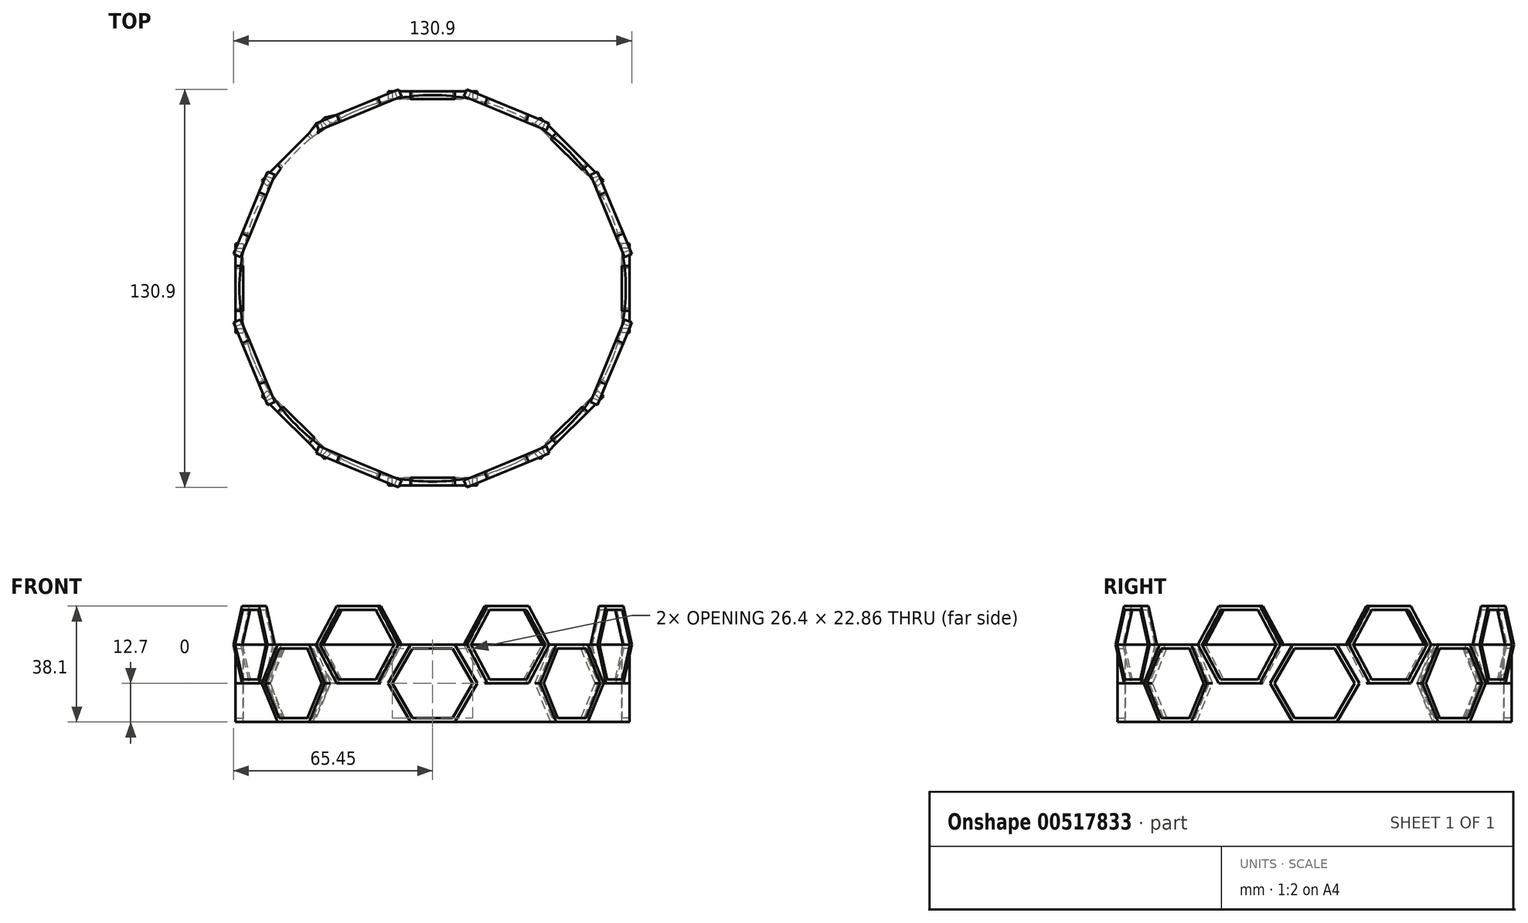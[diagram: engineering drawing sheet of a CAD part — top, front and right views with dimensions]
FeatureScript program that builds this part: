
annotation { "Feature Type Name" : "Feature", "Feature Type Description" : "" }
export const myFeature = defineFeature(function(context is Context, id is Id, definition is map)
    precondition{}
    {
        {
            var Q0;
            Q0=qCreatedBy(makeId("Top.planeOp"),FACE);
            var sketch = newSketch(context, id + "F0", { "sketchPlane" : qUnion([Q0])});
            skCircle(sketch, "E0", {"center": v(0, 0) * mm, "radius": 63.5 * mm});
            skLineSegment(sketch, "E1", {"start": v(-60.89, -18.03) * mm, "end": v(19.66, 60.38) * mm});
            skSolve(sketch);
        }
        {
            var Q0;
            {var subQ0=sQuery(id+"F0.wireOp",EDGE,"E1");Q0=makeQuery(id+"F0.imprint","IMPRINT",FACE,{"disambiguationData":[TD([[makeQuery(id+"F0.imprint","IMPRINT",EDGE,{"derivedFrom":subQ0}),1.0]])]});}
            var Q1;
            {var subQ0=sQuery(id+"F0.wireOp",EDGE,"E1");Q1=makeQuery(id+"F0.imprint","IMPRINT",FACE,{"disambiguationData":[TD([[makeQuery(id+"F0.imprint","IMPRINT",EDGE,{"derivedFrom":subQ0}),-1.0]])]});}
            extrude(context, id + "F1", {"entities" : qUnion([Q0, Q1]), "depth" : 25.4 * mm, "offsetDistance" : 25.4 * mm});
        }
        {
            var Q0;
            Q0=makeQuery(id+"F1.opExtrude","CAP_FACE",FACE,{"disambiguationData":[OSD([sQuery(id+"F0.wireOp",EDGE,"E0")])],"isStart":true});
            var sketch = newSketch(context, id + "F2", { "sketchPlane" : qUnion([Q0])});
            skLineSegment(sketch, "E2", {"start": v(0, 0) * mm, "end": v(63.5, 0) * mm});
            skSolve(sketch);
        }
        {
            var Q0;
            Q0=sQuery(id+"F2.wireOp",VERTEX,"E2.end");
            var Q1;
            Q1=sQuery(id+"F2.wireOp",EDGE,"E2");
            cPlane(context, id + "F3", {"entities" : qUnion([Q0, Q1]), "cplaneType" : CPlaneType.LINE_POINT, "offset" : 25.4 * mm, "width" : 152.4 * mm, "height" : 152.4 * mm});
        }
        {
            var Q0;
            Q0=qCreatedBy(id+"F3.planeOp",FACE);
            var sketch = newSketch(context, id + "F4", { "sketchPlane" : qUnion([Q0])});
            skPoint(sketch, "E3", {"position": v(0, 12.7) * mm});
            skCircle(sketch, "E4.cCircle", {"center": v(0, 12.7) * mm, "radius": 12.7 * mm, "construction": true});
            skLineSegment(sketch, "E4.0", {"start": v(7.33, 25.4) * mm, "end": v(14.66, 12.7) * mm});
            skLineSegment(sketch, "E4.1", {"start": v(14.66, 12.7) * mm, "end": v(7.33, 0) * mm});
            skLineSegment(sketch, "E4.2", {"start": v(7.33, 0) * mm, "end": v(-7.33, 0) * mm});
            skLineSegment(sketch, "E4.3", {"start": v(-7.33, 0) * mm, "end": v(-14.66, 12.7) * mm});
            skLineSegment(sketch, "E4.4", {"start": v(-14.66, 12.7) * mm, "end": v(-7.33, 25.4) * mm});
            skLineSegment(sketch, "E4.5", {"start": v(-7.33, 25.4) * mm, "end": v(7.33, 25.4) * mm});
            skPoint(sketch, "E4.0.midPoint", {"position": v(11, 19.05) * mm});
            skPoint(sketch, "E5", {"position": v(0, 0) * mm});
            skCircle(sketch, "E6.cCircle", {"center": v(0, 12.7) * mm, "radius": 13.2 * mm, "construction": true});
            skLineSegment(sketch, "E6.0", {"start": v(6.6, 1.27) * mm, "end": v(-6.6, 1.27) * mm});
            skLineSegment(sketch, "E6.1", {"start": v(-6.6, 1.27) * mm, "end": v(-13.2, 12.7) * mm});
            skLineSegment(sketch, "E6.2", {"start": v(-13.2, 12.7) * mm, "end": v(-6.6, 24.13) * mm});
            skLineSegment(sketch, "E6.3", {"start": v(-6.6, 24.13) * mm, "end": v(6.6, 24.13) * mm});
            skLineSegment(sketch, "E6.4", {"start": v(6.6, 24.13) * mm, "end": v(13.2, 12.7) * mm});
            skLineSegment(sketch, "E6.5", {"start": v(13.2, 12.7) * mm, "end": v(6.6, 1.27) * mm});
            skSolve(sketch);
        }
        {
            var Q0;
            Q0=makeQuery(id+"F4.imprint","IMPRINT",FACE,{"disambiguationData":[TD([[makeQuery(id+"F4.imprint","IMPRINT",EDGE,{"derivedFrom":sQuery(id+"F4.wireOp",EDGE,"E4.0")}),-1.0]])]});
            extrude(context, id + "F5", {"entities" : qUnion([Q0]), "depth" : 1.27 * mm, "offsetDistance" : 25.4 * mm, "hasSecondDirection" : true, "secondDirectionOppositeDirection" : true, "secondDirectionDepth" : 1.27 * mm});
        }
        {
            var Q0;
            Q0=qCreatedBy(makeId("Front.planeOp"),FACE);
            var sketch = newSketch(context, id + "F6", { "sketchPlane" : qUnion([Q0])});
            skLineSegment(sketch, "E7", {"start": v(0, 0) * mm, "end": v(0, 27.25) * mm});
            skSolve(sketch);
        }
        {
            var Q0;
            Q0=makeQuery(id+"F5.opExtrude","SWEPT_BODY",BODY,{"disambiguationData":[OSD([sQuery(id+"F4.wireOp",EDGE,"E4.0"),sQuery(id+"F4.wireOp",EDGE,"E4.1"),sQuery(id+"F4.wireOp",EDGE,"E4.2"),sQuery(id+"F4.wireOp",EDGE,"E4.3"),sQuery(id+"F4.wireOp",EDGE,"E4.4"),sQuery(id+"F4.wireOp",EDGE,"E4.5"),sQuery(id+"F4.wireOp",EDGE,"E6.0"),sQuery(id+"F4.wireOp",EDGE,"E6.1"),sQuery(id+"F4.wireOp",EDGE,"E6.2"),sQuery(id+"F4.wireOp",EDGE,"E6.3"),sQuery(id+"F4.wireOp",EDGE,"E6.4"),sQuery(id+"F4.wireOp",EDGE,"E6.5")])]});
            var Q1;
            Q1=sQuery(id+"F6.wireOp",EDGE,"E7");
            circularPattern(context, id + "F7", {"entities" : qUnion([Q0]), "axis" : qUnion([Q1]), "angle" : 360 * degree, "instanceCount" : 8, "equalSpace" : true});
        }
        {
            var Q0;
            Q0=makeQuery(id+"F7.opPattern","COPY",BODY,{"derivedFrom":makeQuery(id+"F5.opExtrude","SWEPT_BODY",BODY,{"disambiguationData":[OSD([sQuery(id+"F4.wireOp",EDGE,"E4.0"),sQuery(id+"F4.wireOp",EDGE,"E4.1"),sQuery(id+"F4.wireOp",EDGE,"E4.2"),sQuery(id+"F4.wireOp",EDGE,"E4.3"),sQuery(id+"F4.wireOp",EDGE,"E4.4"),sQuery(id+"F4.wireOp",EDGE,"E4.5"),sQuery(id+"F4.wireOp",EDGE,"E6.0"),sQuery(id+"F4.wireOp",EDGE,"E6.1"),sQuery(id+"F4.wireOp",EDGE,"E6.2"),sQuery(id+"F4.wireOp",EDGE,"E6.3"),sQuery(id+"F4.wireOp",EDGE,"E6.4"),sQuery(id+"F4.wireOp",EDGE,"E6.5")])]}),"instanceName":"2"});
            var Q1;
            Q1=makeQuery(id+"F7.opPattern","COPY",BODY,{"derivedFrom":makeQuery(id+"F5.opExtrude","SWEPT_BODY",BODY,{"disambiguationData":[OSD([sQuery(id+"F4.wireOp",EDGE,"E4.0"),sQuery(id+"F4.wireOp",EDGE,"E4.1"),sQuery(id+"F4.wireOp",EDGE,"E4.2"),sQuery(id+"F4.wireOp",EDGE,"E4.3"),sQuery(id+"F4.wireOp",EDGE,"E4.4"),sQuery(id+"F4.wireOp",EDGE,"E4.5"),sQuery(id+"F4.wireOp",EDGE,"E6.0"),sQuery(id+"F4.wireOp",EDGE,"E6.1"),sQuery(id+"F4.wireOp",EDGE,"E6.2"),sQuery(id+"F4.wireOp",EDGE,"E6.3"),sQuery(id+"F4.wireOp",EDGE,"E6.4"),sQuery(id+"F4.wireOp",EDGE,"E6.5")])]}),"instanceName":"1"});
            var Q2;
            Q2=makeQuery(id+"F7.opPattern","COPY",BODY,{"derivedFrom":makeQuery(id+"F5.opExtrude","SWEPT_BODY",BODY,{"disambiguationData":[OSD([sQuery(id+"F4.wireOp",EDGE,"E4.0"),sQuery(id+"F4.wireOp",EDGE,"E4.1"),sQuery(id+"F4.wireOp",EDGE,"E4.2"),sQuery(id+"F4.wireOp",EDGE,"E4.3"),sQuery(id+"F4.wireOp",EDGE,"E4.4"),sQuery(id+"F4.wireOp",EDGE,"E4.5"),sQuery(id+"F4.wireOp",EDGE,"E6.0"),sQuery(id+"F4.wireOp",EDGE,"E6.1"),sQuery(id+"F4.wireOp",EDGE,"E6.2"),sQuery(id+"F4.wireOp",EDGE,"E6.3"),sQuery(id+"F4.wireOp",EDGE,"E6.4"),sQuery(id+"F4.wireOp",EDGE,"E6.5")])]}),"instanceName":"3"});
            var Q3;
            Q3=makeQuery(id+"F5.opExtrude","SWEPT_BODY",BODY,{"disambiguationData":[OSD([sQuery(id+"F4.wireOp",EDGE,"E4.0"),sQuery(id+"F4.wireOp",EDGE,"E4.1"),sQuery(id+"F4.wireOp",EDGE,"E4.2"),sQuery(id+"F4.wireOp",EDGE,"E4.3"),sQuery(id+"F4.wireOp",EDGE,"E4.4"),sQuery(id+"F4.wireOp",EDGE,"E4.5"),sQuery(id+"F4.wireOp",EDGE,"E6.0"),sQuery(id+"F4.wireOp",EDGE,"E6.1"),sQuery(id+"F4.wireOp",EDGE,"E6.2"),sQuery(id+"F4.wireOp",EDGE,"E6.3"),sQuery(id+"F4.wireOp",EDGE,"E6.4"),sQuery(id+"F4.wireOp",EDGE,"E6.5")])]});
            var Q4;
            Q4=makeQuery(id+"F7.opPattern","COPY",BODY,{"derivedFrom":makeQuery(id+"F5.opExtrude","SWEPT_BODY",BODY,{"disambiguationData":[OSD([sQuery(id+"F4.wireOp",EDGE,"E4.0"),sQuery(id+"F4.wireOp",EDGE,"E4.1"),sQuery(id+"F4.wireOp",EDGE,"E4.2"),sQuery(id+"F4.wireOp",EDGE,"E4.3"),sQuery(id+"F4.wireOp",EDGE,"E4.4"),sQuery(id+"F4.wireOp",EDGE,"E4.5"),sQuery(id+"F4.wireOp",EDGE,"E6.0"),sQuery(id+"F4.wireOp",EDGE,"E6.1"),sQuery(id+"F4.wireOp",EDGE,"E6.2"),sQuery(id+"F4.wireOp",EDGE,"E6.3"),sQuery(id+"F4.wireOp",EDGE,"E6.4"),sQuery(id+"F4.wireOp",EDGE,"E6.5")])]}),"instanceName":"4"});
            var Q5;
            Q5=makeQuery(id+"F7.opPattern","COPY",BODY,{"derivedFrom":makeQuery(id+"F5.opExtrude","SWEPT_BODY",BODY,{"disambiguationData":[OSD([sQuery(id+"F4.wireOp",EDGE,"E4.0"),sQuery(id+"F4.wireOp",EDGE,"E4.1"),sQuery(id+"F4.wireOp",EDGE,"E4.2"),sQuery(id+"F4.wireOp",EDGE,"E4.3"),sQuery(id+"F4.wireOp",EDGE,"E4.4"),sQuery(id+"F4.wireOp",EDGE,"E4.5"),sQuery(id+"F4.wireOp",EDGE,"E6.0"),sQuery(id+"F4.wireOp",EDGE,"E6.1"),sQuery(id+"F4.wireOp",EDGE,"E6.2"),sQuery(id+"F4.wireOp",EDGE,"E6.3"),sQuery(id+"F4.wireOp",EDGE,"E6.4"),sQuery(id+"F4.wireOp",EDGE,"E6.5")])]}),"instanceName":"5"});
            var Q6;
            Q6=makeQuery(id+"F7.opPattern","COPY",BODY,{"derivedFrom":makeQuery(id+"F5.opExtrude","SWEPT_BODY",BODY,{"disambiguationData":[OSD([sQuery(id+"F4.wireOp",EDGE,"E4.0"),sQuery(id+"F4.wireOp",EDGE,"E4.1"),sQuery(id+"F4.wireOp",EDGE,"E4.2"),sQuery(id+"F4.wireOp",EDGE,"E4.3"),sQuery(id+"F4.wireOp",EDGE,"E4.4"),sQuery(id+"F4.wireOp",EDGE,"E4.5"),sQuery(id+"F4.wireOp",EDGE,"E6.0"),sQuery(id+"F4.wireOp",EDGE,"E6.1"),sQuery(id+"F4.wireOp",EDGE,"E6.2"),sQuery(id+"F4.wireOp",EDGE,"E6.3"),sQuery(id+"F4.wireOp",EDGE,"E6.4"),sQuery(id+"F4.wireOp",EDGE,"E6.5")])]}),"instanceName":"6"});
            var Q7;
            Q7=makeQuery(id+"F7.opPattern","COPY",BODY,{"derivedFrom":makeQuery(id+"F5.opExtrude","SWEPT_BODY",BODY,{"disambiguationData":[OSD([sQuery(id+"F4.wireOp",EDGE,"E4.0"),sQuery(id+"F4.wireOp",EDGE,"E4.1"),sQuery(id+"F4.wireOp",EDGE,"E4.2"),sQuery(id+"F4.wireOp",EDGE,"E4.3"),sQuery(id+"F4.wireOp",EDGE,"E4.4"),sQuery(id+"F4.wireOp",EDGE,"E4.5"),sQuery(id+"F4.wireOp",EDGE,"E6.0"),sQuery(id+"F4.wireOp",EDGE,"E6.1"),sQuery(id+"F4.wireOp",EDGE,"E6.2"),sQuery(id+"F4.wireOp",EDGE,"E6.3"),sQuery(id+"F4.wireOp",EDGE,"E6.4"),sQuery(id+"F4.wireOp",EDGE,"E6.5")])]}),"instanceName":"7"});
            transform(context, id + "F8", {"entities" : qUnion([Q0, Q1, Q2, Q3, Q4, Q5, Q6, Q7]), "transformType" : TransformType.TRANSLATION_3D, "dx" : 0 * mm, "dy" : 0 * mm, "dz" : 12.7 * mm, "makeCopy" : true});
        }
        {
            var Q0;
            Q0=makeQuery(id+"F8.opPattern","COPY",BODY,{"derivedFrom":makeQuery(id+"F7.opPattern","COPY",BODY,{"derivedFrom":makeQuery(id+"F5.opExtrude","SWEPT_BODY",BODY,{"disambiguationData":[OSD([sQuery(id+"F4.wireOp",EDGE,"E4.0"),sQuery(id+"F4.wireOp",EDGE,"E4.1"),sQuery(id+"F4.wireOp",EDGE,"E4.2"),sQuery(id+"F4.wireOp",EDGE,"E4.3"),sQuery(id+"F4.wireOp",EDGE,"E4.4"),sQuery(id+"F4.wireOp",EDGE,"E4.5"),sQuery(id+"F4.wireOp",EDGE,"E6.0"),sQuery(id+"F4.wireOp",EDGE,"E6.1"),sQuery(id+"F4.wireOp",EDGE,"E6.2"),sQuery(id+"F4.wireOp",EDGE,"E6.3"),sQuery(id+"F4.wireOp",EDGE,"E6.4"),sQuery(id+"F4.wireOp",EDGE,"E6.5")])]}),"instanceName":"3"}),"instanceName":"1"});
            var Q1;
            Q1=makeQuery(id+"F8.opPattern","COPY",BODY,{"derivedFrom":makeQuery(id+"F7.opPattern","COPY",BODY,{"derivedFrom":makeQuery(id+"F5.opExtrude","SWEPT_BODY",BODY,{"disambiguationData":[OSD([sQuery(id+"F4.wireOp",EDGE,"E4.0"),sQuery(id+"F4.wireOp",EDGE,"E4.1"),sQuery(id+"F4.wireOp",EDGE,"E4.2"),sQuery(id+"F4.wireOp",EDGE,"E4.3"),sQuery(id+"F4.wireOp",EDGE,"E4.4"),sQuery(id+"F4.wireOp",EDGE,"E4.5"),sQuery(id+"F4.wireOp",EDGE,"E6.0"),sQuery(id+"F4.wireOp",EDGE,"E6.1"),sQuery(id+"F4.wireOp",EDGE,"E6.2"),sQuery(id+"F4.wireOp",EDGE,"E6.3"),sQuery(id+"F4.wireOp",EDGE,"E6.4"),sQuery(id+"F4.wireOp",EDGE,"E6.5")])]}),"instanceName":"2"}),"instanceName":"1"});
            var Q2;
            Q2=makeQuery(id+"F8.opPattern","COPY",BODY,{"derivedFrom":makeQuery(id+"F7.opPattern","COPY",BODY,{"derivedFrom":makeQuery(id+"F5.opExtrude","SWEPT_BODY",BODY,{"disambiguationData":[OSD([sQuery(id+"F4.wireOp",EDGE,"E4.0"),sQuery(id+"F4.wireOp",EDGE,"E4.1"),sQuery(id+"F4.wireOp",EDGE,"E4.2"),sQuery(id+"F4.wireOp",EDGE,"E4.3"),sQuery(id+"F4.wireOp",EDGE,"E4.4"),sQuery(id+"F4.wireOp",EDGE,"E4.5"),sQuery(id+"F4.wireOp",EDGE,"E6.0"),sQuery(id+"F4.wireOp",EDGE,"E6.1"),sQuery(id+"F4.wireOp",EDGE,"E6.2"),sQuery(id+"F4.wireOp",EDGE,"E6.3"),sQuery(id+"F4.wireOp",EDGE,"E6.4"),sQuery(id+"F4.wireOp",EDGE,"E6.5")])]}),"instanceName":"1"}),"instanceName":"1"});
            var Q3;
            Q3=makeQuery(id+"F8.opPattern","COPY",BODY,{"derivedFrom":makeQuery(id+"F5.opExtrude","SWEPT_BODY",BODY,{"disambiguationData":[OSD([sQuery(id+"F4.wireOp",EDGE,"E4.0"),sQuery(id+"F4.wireOp",EDGE,"E4.1"),sQuery(id+"F4.wireOp",EDGE,"E4.2"),sQuery(id+"F4.wireOp",EDGE,"E4.3"),sQuery(id+"F4.wireOp",EDGE,"E4.4"),sQuery(id+"F4.wireOp",EDGE,"E4.5"),sQuery(id+"F4.wireOp",EDGE,"E6.0"),sQuery(id+"F4.wireOp",EDGE,"E6.1"),sQuery(id+"F4.wireOp",EDGE,"E6.2"),sQuery(id+"F4.wireOp",EDGE,"E6.3"),sQuery(id+"F4.wireOp",EDGE,"E6.4"),sQuery(id+"F4.wireOp",EDGE,"E6.5")])]}),"instanceName":"1"});
            var Q4;
            Q4=makeQuery(id+"F8.opPattern","COPY",BODY,{"derivedFrom":makeQuery(id+"F7.opPattern","COPY",BODY,{"derivedFrom":makeQuery(id+"F5.opExtrude","SWEPT_BODY",BODY,{"disambiguationData":[OSD([sQuery(id+"F4.wireOp",EDGE,"E4.0"),sQuery(id+"F4.wireOp",EDGE,"E4.1"),sQuery(id+"F4.wireOp",EDGE,"E4.2"),sQuery(id+"F4.wireOp",EDGE,"E4.3"),sQuery(id+"F4.wireOp",EDGE,"E4.4"),sQuery(id+"F4.wireOp",EDGE,"E4.5"),sQuery(id+"F4.wireOp",EDGE,"E6.0"),sQuery(id+"F4.wireOp",EDGE,"E6.1"),sQuery(id+"F4.wireOp",EDGE,"E6.2"),sQuery(id+"F4.wireOp",EDGE,"E6.3"),sQuery(id+"F4.wireOp",EDGE,"E6.4"),sQuery(id+"F4.wireOp",EDGE,"E6.5")])]}),"instanceName":"7"}),"instanceName":"1"});
            var Q5;
            Q5=makeQuery(id+"F8.opPattern","COPY",BODY,{"derivedFrom":makeQuery(id+"F7.opPattern","COPY",BODY,{"derivedFrom":makeQuery(id+"F5.opExtrude","SWEPT_BODY",BODY,{"disambiguationData":[OSD([sQuery(id+"F4.wireOp",EDGE,"E4.0"),sQuery(id+"F4.wireOp",EDGE,"E4.1"),sQuery(id+"F4.wireOp",EDGE,"E4.2"),sQuery(id+"F4.wireOp",EDGE,"E4.3"),sQuery(id+"F4.wireOp",EDGE,"E4.4"),sQuery(id+"F4.wireOp",EDGE,"E4.5"),sQuery(id+"F4.wireOp",EDGE,"E6.0"),sQuery(id+"F4.wireOp",EDGE,"E6.1"),sQuery(id+"F4.wireOp",EDGE,"E6.2"),sQuery(id+"F4.wireOp",EDGE,"E6.3"),sQuery(id+"F4.wireOp",EDGE,"E6.4"),sQuery(id+"F4.wireOp",EDGE,"E6.5")])]}),"instanceName":"6"}),"instanceName":"1"});
            var Q6;
            Q6=makeQuery(id+"F8.opPattern","COPY",BODY,{"derivedFrom":makeQuery(id+"F7.opPattern","COPY",BODY,{"derivedFrom":makeQuery(id+"F5.opExtrude","SWEPT_BODY",BODY,{"disambiguationData":[OSD([sQuery(id+"F4.wireOp",EDGE,"E4.0"),sQuery(id+"F4.wireOp",EDGE,"E4.1"),sQuery(id+"F4.wireOp",EDGE,"E4.2"),sQuery(id+"F4.wireOp",EDGE,"E4.3"),sQuery(id+"F4.wireOp",EDGE,"E4.4"),sQuery(id+"F4.wireOp",EDGE,"E4.5"),sQuery(id+"F4.wireOp",EDGE,"E6.0"),sQuery(id+"F4.wireOp",EDGE,"E6.1"),sQuery(id+"F4.wireOp",EDGE,"E6.2"),sQuery(id+"F4.wireOp",EDGE,"E6.3"),sQuery(id+"F4.wireOp",EDGE,"E6.4"),sQuery(id+"F4.wireOp",EDGE,"E6.5")])]}),"instanceName":"5"}),"instanceName":"1"});
            var Q7;
            Q7=makeQuery(id+"F8.opPattern","COPY",BODY,{"derivedFrom":makeQuery(id+"F7.opPattern","COPY",BODY,{"derivedFrom":makeQuery(id+"F5.opExtrude","SWEPT_BODY",BODY,{"disambiguationData":[OSD([sQuery(id+"F4.wireOp",EDGE,"E4.0"),sQuery(id+"F4.wireOp",EDGE,"E4.1"),sQuery(id+"F4.wireOp",EDGE,"E4.2"),sQuery(id+"F4.wireOp",EDGE,"E4.3"),sQuery(id+"F4.wireOp",EDGE,"E4.4"),sQuery(id+"F4.wireOp",EDGE,"E4.5"),sQuery(id+"F4.wireOp",EDGE,"E6.0"),sQuery(id+"F4.wireOp",EDGE,"E6.1"),sQuery(id+"F4.wireOp",EDGE,"E6.2"),sQuery(id+"F4.wireOp",EDGE,"E6.3"),sQuery(id+"F4.wireOp",EDGE,"E6.4"),sQuery(id+"F4.wireOp",EDGE,"E6.5")])]}),"instanceName":"4"}),"instanceName":"1"});
            var Q8;
            Q8=sQuery(id+"F6.wireOp",EDGE,"E7");
            transform(context, id + "F9", {"entities" : qUnion([Q0, Q1, Q2, Q3, Q4, Q5, Q6, Q7]), "transformType" : TransformType.ROTATION, "transformAxis" : qUnion([Q8]), "angle" : 22.5 * degree, "makeCopy" : false});
        }
        {
            var Q1;
            Q1=makeQuery(id+"F8.opPattern","COPY",FACE,{"derivedFrom":makeQuery(id+"F7.opPattern","COPY",FACE,{"derivedFrom":makeQuery(id+"F5.opExtrude","SWEPT_FACE",FACE,{"disambiguationData":[OSD([sQuery(id+"F4.wireOp",EDGE,"E4.1")])]}),"instanceName":"2"}),"instanceName":"1"});
            var Q2;
            Q2=makeQuery(id+"F7.opPattern","COPY",FACE,{"derivedFrom":makeQuery(id+"F5.opExtrude","SWEPT_FACE",FACE,{"disambiguationData":[OSD([sQuery(id+"F4.wireOp",EDGE,"E4.4")])]}),"instanceName":"3"});
            loft(context, id + "F10", {"operationType" : NewBodyOperationType.ADD, "sheetProfilesArray" : [{ "sheetProfileEntities" : qUnion([Q1]) }, { "sheetProfileEntities" : qUnion([Q2]) }]});
        }
    });
